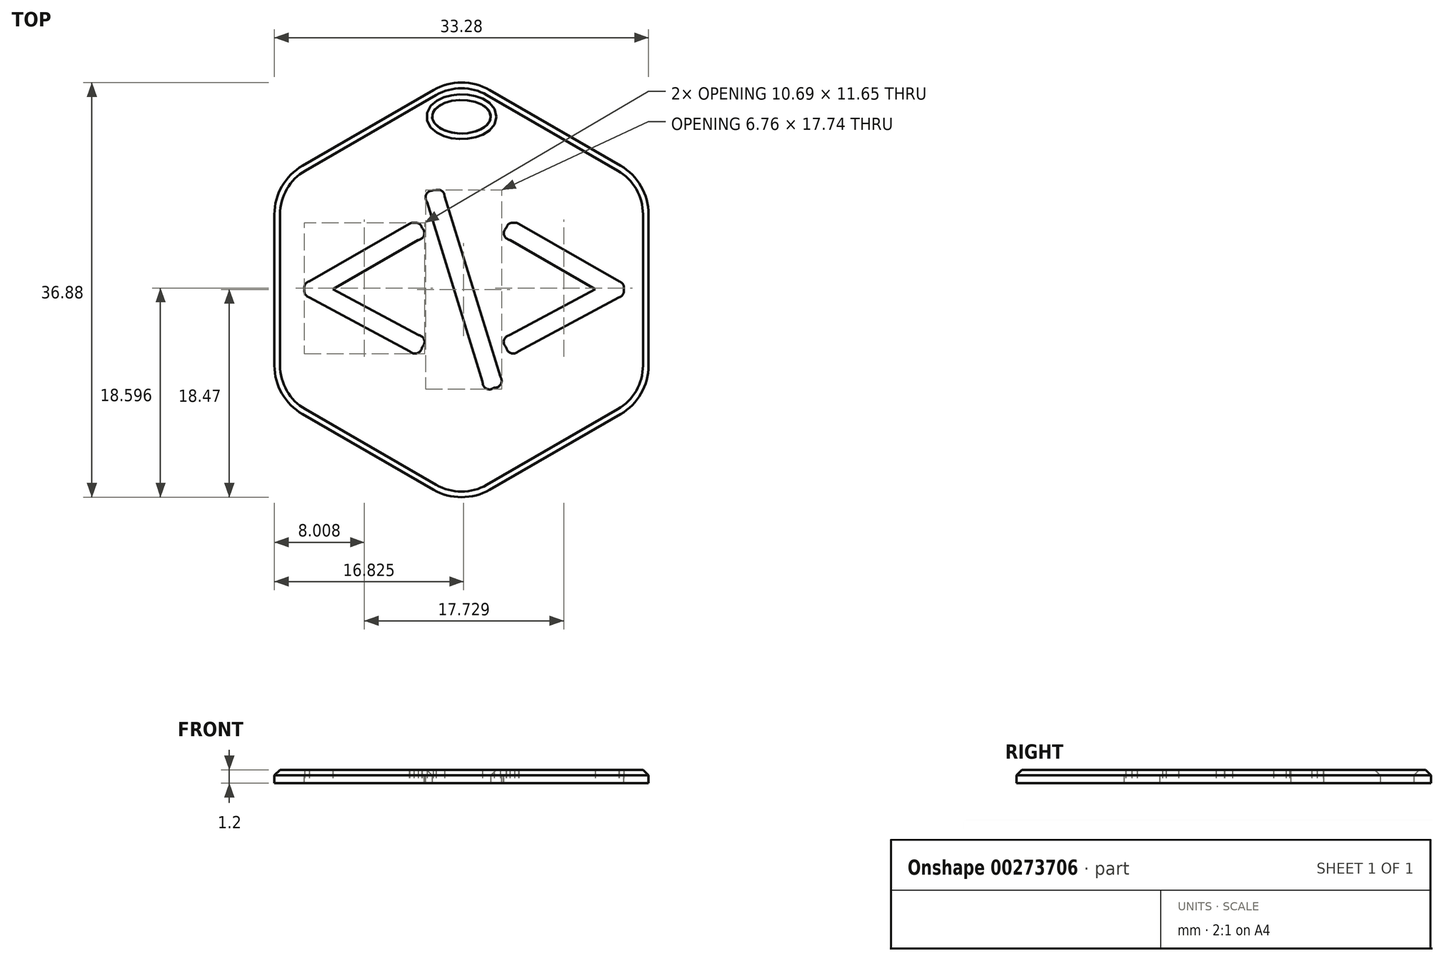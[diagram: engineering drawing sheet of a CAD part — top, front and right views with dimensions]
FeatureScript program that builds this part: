
annotation { "Feature Type Name" : "Feature", "Feature Type Description" : "" }
export const myFeature = defineFeature(function(context is Context, id is Id, definition is map)
    precondition{}
    {
        {
            var Q0;
            Q0=qCreatedBy(makeId("Top.planeOp"),FACE);
            var sketch = newSketch(context, id + "F0", { "sketchPlane" : qUnion([Q0])});
            skCircle(sketch, "E0.cCircle", {"center": v(0, 0) * mm, "radius": 16.64 * mm, "construction": true});
            skLineSegment(sketch, "E0.0", {"start": v(16.64, 6.72) * mm, "end": v(16.64, -6.72) * mm});
            skLineSegment(sketch, "E0.1", {"start": v(14.14, -11.05) * mm, "end": v(2.5, -17.77) * mm});
            skLineSegment(sketch, "E0.2", {"start": v(-2.5, -17.77) * mm, "end": v(-14.14, -11.05) * mm});
            skLineSegment(sketch, "E0.3", {"start": v(-16.64, -6.72) * mm, "end": v(-16.64, 6.72) * mm});
            skLineSegment(sketch, "E0.4", {"start": v(-14.14, 11.05) * mm, "end": v(-2.5, 17.77) * mm});
            skLineSegment(sketch, "E0.5", {"start": v(2.5, 17.77) * mm, "end": v(14.14, 11.05) * mm});
            skPoint(sketch, "E0.0.midPoint", {"position": v(16.64, 0) * mm});
            skPoint(sketch, "E1.visualSharp", {"position": v(-16.64, 9.6) * mm});
            skArc(sketch, "E1.filletArc", {"start": v(-14.14, 11.05) * mm, "mid": v(-15.97, 9.22) * mm, "end": v(-16.64, 6.72) * mm});
            skPoint(sketch, "E2.visualSharp", {"position": v(0, 19.22) * mm});
            skArc(sketch, "E2.filletArc", {"start": v(2.5, 17.77) * mm, "mid": v(0, 18.44) * mm, "end": v(-2.5, 17.77) * mm});
            skPoint(sketch, "E3.visualSharp", {"position": v(16.64, 9.6) * mm});
            skArc(sketch, "E3.filletArc", {"start": v(16.64, 6.72) * mm, "mid": v(15.97, 9.22) * mm, "end": v(14.14, 11.05) * mm});
            skPoint(sketch, "E4.visualSharp", {"position": v(16.64, -9.6) * mm});
            skArc(sketch, "E4.filletArc", {"start": v(14.14, -11.05) * mm, "mid": v(15.97, -9.22) * mm, "end": v(16.64, -6.72) * mm});
            skPoint(sketch, "E5.visualSharp", {"position": v(0, -19.22) * mm});
            skArc(sketch, "E5.filletArc", {"start": v(-2.5, -17.77) * mm, "mid": v(0, -18.44) * mm, "end": v(2.5, -17.77) * mm});
            skPoint(sketch, "E6.visualSharp", {"position": v(-16.64, -9.6) * mm});
            skArc(sketch, "E6.filletArc", {"start": v(-16.64, -6.72) * mm, "mid": v(-15.97, -9.22) * mm, "end": v(-14.14, -11.05) * mm});
            skPoint(sketch, "E7.visualSharp", {"position": v(-14.64, 8.45) * mm});
            skPoint(sketch, "E8.visualSharp", {"position": v(0, 16.9) * mm});
            skPoint(sketch, "E9.visualSharp", {"position": v(14.64, 8.45) * mm});
            skPoint(sketch, "E10.visualSharp", {"position": v(14.64, -8.45) * mm});
            skPoint(sketch, "E11.visualSharp", {"position": v(0, -16.9) * mm});
            skPoint(sketch, "E12.visualSharp", {"position": v(-14.64, -8.45) * mm});
            skEllipse(sketch, "E13", {"center": v(0, 15.41) * mm, "majorRadius": 2.6 * mm, "minorRadius": 1.5 * mm, "majorAxis": v(1, 0)});
            skFitSpline(sketch, "E14", {"points": [v(-2.87, 8.62) * mm, v(-2.95, 8.62) * mm, v(-3.03, 8.61) * mm, v(-3.11, 8.59) * mm]});
            skFitSpline(sketch, "E15", {"points": [v(-2.52, 8.85) * mm, v(-2.96, 8.72) * mm, v(-3.2, 8.26) * mm, v(-3.06, 7.82) * mm]});
            skFitSpline(sketch, "E16", {"points": [v(1.87, -8.17) * mm, v(2, -8.6) * mm, v(2.46, -8.85) * mm, v(2.9, -8.71) * mm]});
            skFitSpline(sketch, "E17", {"points": [v(2.9, -8.71) * mm, v(3.33, -8.58) * mm, v(3.57, -8.12) * mm, v(3.44, -7.68) * mm]});
            skLineSegment(sketch, "E18", {"start": v(-3.06, 7.82) * mm, "end": v(1.87, -8.17) * mm});
            skFitSpline(sketch, "E19", {"points": [v(-1.5, 8.3) * mm, v(-1.6, 8.66) * mm, v(-1.93, 8.89) * mm, v(-2.28, 8.89) * mm]});
            skFitSpline(sketch, "E20", {"points": [v(4.71, 5.97) * mm, v(4.43, 5.97) * mm, v(4.15, 5.82) * mm, v(4, 5.55) * mm]});
            skFitSpline(sketch, "E21", {"points": [v(4, 5.55) * mm, v(3.77, 5.16) * mm, v(3.9, 4.66) * mm, v(4.3, 4.43) * mm]});
            skLineSegment(sketch, "E22", {"start": v(3.44, -7.68) * mm, "end": v(-1.5, 8.3) * mm});
            skFitSpline(sketch, "E23", {"points": [v(4.3, -4) * mm, v(3.9, -4.21) * mm, v(3.76, -4.71) * mm, v(3.97, -5.11) * mm]});
            skFitSpline(sketch, "E24", {"points": [v(3.97, -5.11) * mm, v(4.19, -5.51) * mm, v(4.69, -5.66) * mm, v(5.09, -5.45) * mm]});
            skLineSegment(sketch, "E25", {"start": v(4.3, 4.43) * mm, "end": v(11.9, 0.08) * mm});
            skLineSegment(sketch, "E26", {"start": v(11.9, 0.08) * mm, "end": v(4.3, -4) * mm});
            skFitSpline(sketch, "E27", {"points": [v(14, -0.67) * mm, v(14.25, -0.53) * mm, v(14.42, -0.26) * mm, v(14.43, 0.04) * mm]});
            skFitSpline(sketch, "E28", {"points": [v(14.43, 0.04) * mm, v(14.43, 0.34) * mm, v(14.27, 0.62) * mm, v(14.01, 0.77) * mm]});
            skLineSegment(sketch, "E29", {"start": v(5.09, -5.45) * mm, "end": v(14, -0.67) * mm});
            skFitSpline(sketch, "E30", {"points": [v(5.12, 5.86) * mm, v(4.99, 5.93) * mm, v(4.85, 5.97) * mm, v(4.71, 5.97) * mm]});
            skFitSpline(sketch, "E31", {"points": [v(-4.25, 5.97) * mm, v(-4.38, 5.97) * mm, v(-4.53, 5.93) * mm, v(-4.65, 5.86) * mm]});
            skLineSegment(sketch, "E32", {"start": v(14.01, 0.77) * mm, "end": v(5.12, 5.86) * mm});
            skFitSpline(sketch, "E33", {"points": [v(-13.55, 0.77) * mm, v(-13.8, 0.62) * mm, v(-13.97, 0.34) * mm, v(-13.96, 0.04) * mm]});
            skFitSpline(sketch, "E34", {"points": [v(-13.96, 0.04) * mm, v(-13.96, -0.26) * mm, v(-13.8, -0.53) * mm, v(-13.53, -0.67) * mm]});
            skLineSegment(sketch, "E35", {"start": v(-4.65, 5.86) * mm, "end": v(-13.55, 0.77) * mm});
            skFitSpline(sketch, "E36", {"points": [v(-4.62, -5.45) * mm, v(-4.22, -5.66) * mm, v(-3.72, -5.51) * mm, v(-3.5, -5.11) * mm]});
            skFitSpline(sketch, "E37", {"points": [v(-3.5, -5.11) * mm, v(-3.3, -4.71) * mm, v(-3.44, -4.21) * mm, v(-3.84, -4) * mm]});
            skLineSegment(sketch, "E38", {"start": v(-13.53, -0.67) * mm, "end": v(-4.62, -5.45) * mm});
            skFitSpline(sketch, "E39", {"points": [v(-3.84, 4.43) * mm, v(-3.44, 4.66) * mm, v(-3.3, 5.16) * mm, v(-3.53, 5.55) * mm]});
            skFitSpline(sketch, "E40", {"points": [v(-3.53, 5.55) * mm, v(-3.68, 5.82) * mm, v(-3.96, 5.97) * mm, v(-4.25, 5.97) * mm]});
            skLineSegment(sketch, "E41", {"start": v(-3.84, -4) * mm, "end": v(-11.44, 0.08) * mm});
            skLineSegment(sketch, "E42", {"start": v(-11.44, 0.08) * mm, "end": v(-3.84, 4.43) * mm});
            skLineSegment(sketch, "E43", {"start": v(-2.52, 8.85) * mm, "end": v(-2.28, 8.89) * mm});
            skSolve(sketch);
        }
        {
            var Q0;
            Q0=qSketchRegion(id+"F0",true);
            extrude(context, id + "F1", {"entities" : qUnion([Q0]), "depth" : 1.2 * mm});
        }
        {
            var Q0;
            Q0=makeQuery(id+"F1.opExtrude","CAP_EDGE",EDGE,{"disambiguationData":[OSD([sQuery(id+"F0.wireOp",EDGE,"E0.2")])],"isStart":false});
            chamfer(context, id + "F2", {"entities" : qUnion([Q0]), "width" : 0.5 * mm, "tangentPropagation" : true});
        }
        {
            var Q0;
            Q0=makeQuery(id+"F1.opExtrude","CAP_EDGE",EDGE,{"disambiguationData":[OSD([sQuery(id+"F0.wireOp",EDGE,"E13")])],"isStart":false});
            chamfer(context, id + "F3", {"entities" : qUnion([Q0]), "width" : 0.5 * mm, "tangentPropagation" : true});
        }
    });
